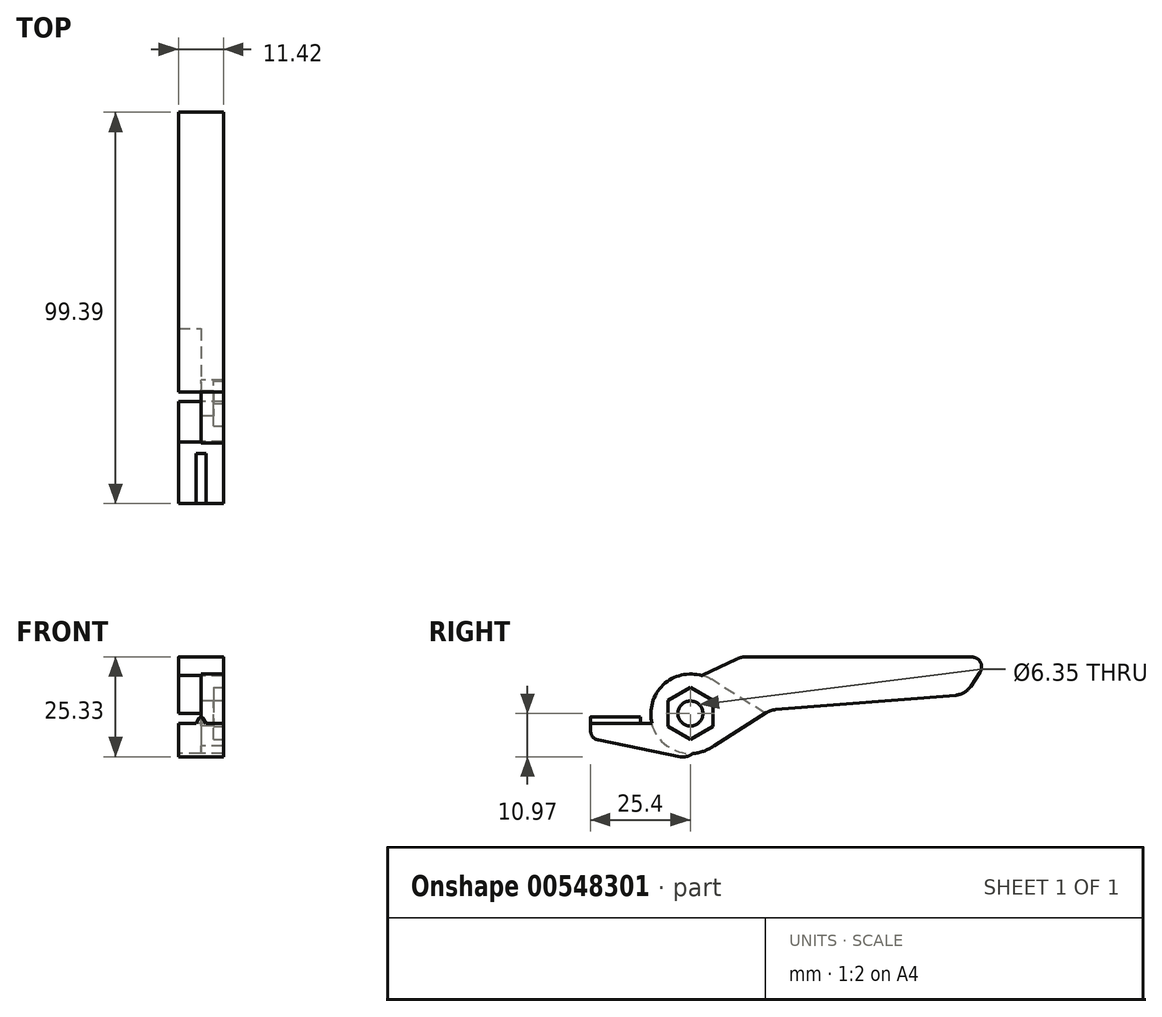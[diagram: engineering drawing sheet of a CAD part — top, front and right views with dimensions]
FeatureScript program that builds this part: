
annotation { "Feature Type Name" : "Feature", "Feature Type Description" : "" }
export const myFeature = defineFeature(function(context is Context, id is Id, definition is map)
    precondition{}
    {
        {
            var Q0;
            Q0=qCreatedBy(makeId("Right.planeOp"),FACE);
            var sketch = newSketch(context, id + "F0", { "sketchPlane" : qUnion([Q0])});
            skCircle(sketch, "E0", {"center": v(0, 0) * mm, "radius": 3.18 * mm});
            skArc(sketch, "E1", {"start": v(10.03, 0) * mm, "mid": v(-1.28, 9.95) * mm, "end": v(-9.7, -2.54) * mm});
            skLineSegment(sketch, "E2", {"start": v(-15.98, -2.54) * mm, "end": v(-8.82, -2.54) * mm});
            skArc(sketch, "E3", {"start": v(-9.84, -2.54) * mm, "mid": v(1.28, -10.08) * mm, "end": v(10.16, 0) * mm});
            skLineSegment(sketch, "E4", {"start": v(8.55, 0) * mm, "end": v(12.43, 0) * mm});
            skPoint(sketch, "E5.orphan", {"position": v(0, -10.03) * mm});
            skSolve(sketch);
        }
        {
            var Q0;
            Q0=qCreatedBy(makeId("Right.planeOp"),FACE);
            var sketch = newSketch(context, id + "F1", { "sketchPlane" : qUnion([Q0])});
            skLineSegment(sketch, "E6", {"start": v(9.3, 0) * mm, "end": v(10.16, 0.07) * mm});
            skLineSegment(sketch, "E7", {"start": v(69.85, 4.85) * mm, "end": v(76.2, 14.36) * mm});
            skCircle(sketch, "E8", {"center": v(0, 0) * mm, "radius": 10.16 * mm, "construction": true});
            skLineSegment(sketch, "E9", {"start": v(0, 0) * mm, "end": v(76.2, 0) * mm, "construction": true});
            skLineSegment(sketch, "E10", {"start": v(76.2, 14.36) * mm, "end": v(12.8, 14.36) * mm});
            skLineSegment(sketch, "E11", {"start": v(12.8, 14.36) * mm, "end": v(2.92, 9.73) * mm});
            skLineSegment(sketch, "E12", {"start": v(76.2, 14.36) * mm, "end": v(76.2, 0) * mm, "construction": true});
            skPoint(sketch, "E13.endSnap0", {"position": v(7.86, 12.04) * mm});
            skLineSegment(sketch, "E14", {"start": v(5.96, -8.23) * mm, "end": v(4.87, -6.63) * mm});
            skLineSegment(sketch, "E15", {"start": v(4.87, -6.63) * mm, "end": v(8.24, 1.75) * mm});
            skLineSegment(sketch, "E16", {"start": v(8.24, 1.75) * mm, "end": v(2.92, 9.73) * mm});
            skLineSegment(sketch, "E17.trimOffspring", {"start": v(20.4, 0.89) * mm, "end": v(69.85, 4.85) * mm});
            skLineSegment(sketch, "E18", {"start": v(20.4, 0.89) * mm, "end": v(5.96, -8.23) * mm});
            skSolve(sketch);
        }
        {
            var Q0;
            Q0 = qSketchRegion(id + "F1", true);
            extrude(context, id + "F2", {"entities" : qUnion([Q0]), "endBound" : BoundingType.SYMMETRIC, "depth" : 11.43 * mm, "offsetDistance" : 25.4 * mm});
        }
        {
            var Q0;
            Q0=makeQuery(id+"F2.opExtrude","SWEPT_EDGE",EDGE,{"disambiguationData":[OSD([sQuery(id+"F1.wireOp",EDGE,"E10"),sQuery(id+"F1.wireOp",EDGE,"E11")])]});
            var Q1;
            Q1=makeQuery(id+"F2.opExtrude","SWEPT_EDGE",EDGE,{"disambiguationData":[OSD([sQuery(id+"F1.wireOp",EDGE,"E7"),sQuery(id+"F1.wireOp",EDGE,"E17.trimOffspring")])]});
            var Q2;
            Q2=makeQuery(id+"F2.opExtrude","SWEPT_EDGE",EDGE,{"disambiguationData":[OSD([sQuery(id+"F1.wireOp",EDGE,"E17.trimOffspring"),sQuery(id+"F1.wireOp",EDGE,"E18")])]});
            fillet(context, id + "F3", {"entities" : qUnion([Q0, Q1, Q2]), "radius" : 5.08 * mm, "tangentPropagation" : true, "allowEdgeOverflow" : false});
        }
        {
            var Q0;
            Q0=makeQuery(id+"F2.opExtrude","SWEPT_EDGE",EDGE,{"disambiguationData":[OSD([sQuery(id+"F1.wireOp",EDGE,"E7"),sQuery(id+"F1.wireOp",EDGE,"E10")])]});
            fillet(context, id + "F4", {"entities" : qUnion([Q0]), "radius" : 2.54 * mm, "tangentPropagation" : true, "allowEdgeOverflow" : false});
        }
        {
            var Q0;
            Q0 = qSketchRegion(id + "F0", true);
            extrude(context, id + "F5", {"entities" : qUnion([Q0]), "operationType" : NewBodyOperationType.ADD, "depth" : 5.7 * mm, "offsetDistance" : 25.4 * mm});
        }
        {
            var Q0;
            Q0=qCreatedBy(makeId("Right.planeOp"),FACE);
            var sketch = newSketch(context, id + "F6", { "sketchPlane" : qUnion([Q0])});
            skArc(sketch, "E19", {"start": v(5.42, 8.6) * mm, "mid": v(-10.16, -0.1) * mm, "end": v(5.57, -8.5) * mm});
            skLineSegment(sketch, "E20", {"start": v(19.06, 0) * mm, "end": v(5.42, 8.6) * mm});
            skLineSegment(sketch, "E21", {"start": v(5.57, -8.5) * mm, "end": v(19.06, 0) * mm});
            skSolve(sketch);
        }
        {
            var Q0;
            Q0 = qSketchRegion(id + "F6", true);
            extrude(context, id + "F7", {"entities" : qUnion([Q0]), "operationType" : NewBodyOperationType.REMOVE, "oppositeDirection" : true, "depth" : 25.4 * mm, "offsetDistance" : 25.4 * mm});
        }
        {
            var Q0;
            Q0=qCreatedBy(makeId("Right.planeOp"),FACE);
            var sketch = newSketch(context, id + "F8", { "sketchPlane" : qUnion([Q0])});
            skCircle(sketch, "E22", {"center": v(0, 0) * mm, "radius": 10.16 * mm});
            skLineSegment(sketch, "E23", {"start": v(-9.84, 2.54) * mm, "end": v(-25.4, 2.54) * mm});
            skLineSegment(sketch, "E24", {"start": v(-25.4, 2.54) * mm, "end": v(-25.4, 6.36) * mm});
            skLineSegment(sketch, "E25", {"start": v(-25.4, 6.36) * mm, "end": v(-2.53, 10.97) * mm});
            skLineSegment(sketch, "E26", {"start": v(-2.53, 10.97) * mm, "end": v(7.5, 10.97) * mm});
            skLineSegment(sketch, "E27", {"start": v(7.5, 10.97) * mm, "end": v(4.02, 9.33) * mm});
            skLineSegment(sketch, "E28", {"start": v(0, 0) * mm, "end": v(-31.38, 0) * mm, "construction": true});
            skLineSegment(sketch, "E29.MirrorCS", {"start": v(-9.84, -2.54) * mm, "end": v(-25.4, -2.54) * mm});
            skLineSegment(sketch, "E30.MirrorCS", {"start": v(-25.4, -2.54) * mm, "end": v(-25.4, -6.36) * mm});
            skLineSegment(sketch, "E31.MirrorCS", {"start": v(-25.4, -6.36) * mm, "end": v(-2.53, -10.97) * mm});
            skLineSegment(sketch, "E32.MirrorCS", {"start": v(-2.53, -10.97) * mm, "end": v(7.5, -10.97) * mm});
            skLineSegment(sketch, "E33.MirrorCS", {"start": v(7.5, -10.97) * mm, "end": v(4.02, -9.33) * mm});
            skLineSegment(sketch, "E34", {"start": v(0.54, -10.15) * mm, "end": v(0.54, -10.97) * mm});
            skSolve(sketch);
        }
        {
            var Q0;
            {var subQ0=sQuery(id+"F8.wireOp",EDGE,"E29.MirrorCS");Q0=makeQuery(id+"F8.imprint","IMPRINT",FACE,{"disambiguationData":[TD([[makeQuery(id+"F8.imprint","IMPRINT",EDGE,{"derivedFrom":subQ0}),1.0]])]});}
            extrude(context, id + "F9", {"entities" : qUnion([Q0]), "operationType" : NewBodyOperationType.ADD, "endBound" : BoundingType.SYMMETRIC, "depth" : 11.43 * mm, "offsetDistance" : 25.4 * mm});
        }
        {
            var Q0;
            Q0=makeQuery(id+"F9.opExtrude","SWEPT_EDGE",EDGE,{"disambiguationData":[OSD([sQuery(id+"F8.wireOp",EDGE,"E32.MirrorCS"),sQuery(id+"F8.wireOp",EDGE,"E34")])]});
            var Q1;
            Q1=makeQuery(id+"F9.opExtrude","SWEPT_EDGE",EDGE,{"disambiguationData":[OSD([sQuery(id+"F8.wireOp",EDGE,"E30.MirrorCS"),sQuery(id+"F8.wireOp",EDGE,"E31.MirrorCS")])]});
            fillet(context, id + "F10", {"entities" : qUnion([Q0, Q1]), "radius" : 2.54 * mm, "tangentPropagation" : true, "allowEdgeOverflow" : false});
        }
        {
            var Q0;
            Q0=makeQuery(id+"F9.opExtrude","SWEPT_FACE",FACE,{"disambiguationData":[OSD([sQuery(id+"F8.wireOp",EDGE,"E30.MirrorCS")])]});
            var sketch = newSketch(context, id + "F11", { "sketchPlane" : qUnion([Q0])});
            skLineSegment(sketch, "E35", {"start": v(-1.27, -2.54) * mm, "end": v(0, -0.41) * mm});
            skLineSegment(sketch, "E36", {"start": v(0, -0.41) * mm, "end": v(1.27, -2.54) * mm});
            skLineSegment(sketch, "E37", {"start": v(1.27, -2.54) * mm, "end": v(-1.27, -2.54) * mm});
            skSolve(sketch);
        }
        {
            var Q0;
            Q0 = qSketchRegion(id + "F11", true);
            extrude(context, id + "F12", {"entities" : qUnion([Q0]), "operationType" : NewBodyOperationType.ADD, "oppositeDirection" : true, "depth" : 12.7 * mm, "offsetDistance" : 25.4 * mm});
        }
        {
            var Q0;
            Q0=makeQuery(id+"F12.opExtrude","SWEPT_EDGE",EDGE,{"disambiguationData":[OSD([sQuery(id+"F11.wireOp",EDGE,"E35"),sQuery(id+"F11.wireOp",EDGE,"E36")])]});
            fillet(context, id + "F13", {"entities" : qUnion([Q0]), "radius" : 0.5 * mm, "tangentPropagation" : true, "allowEdgeOverflow" : false});
        }
        {
            var Q0;
            Q0=makeQuery(id+"F9.boolean.opBoolean","MERGE",FACE,{"derivedFrom":[makeQuery(id+"F5.boolean.opBoolean","MERGE",FACE,{"derivedFrom":[makeQuery(id+"F2.opExtrude","CAP_FACE",FACE,{"disambiguationData":[OSD([sQuery(id+"F1.wireOp",EDGE,"E7"),sQuery(id+"F1.wireOp",EDGE,"E10"),sQuery(id+"F1.wireOp",EDGE,"E11"),sQuery(id+"F1.wireOp",EDGE,"E14"),sQuery(id+"F1.wireOp",EDGE,"E15"),sQuery(id+"F1.wireOp",EDGE,"E16"),sQuery(id+"F1.wireOp",EDGE,"E17.trimOffspring"),sQuery(id+"F1.wireOp",EDGE,"E18")])],"isStart":false}),makeQuery(id+"F5.opExtrude","CAP_FACE",FACE,{"disambiguationData":[OSD([sQuery(id+"F0.wireOp",EDGE,"E0"),sQuery(id+"F0.wireOp",EDGE,"E1")])],"isStart":false})]}),makeQuery(id+"F9.opExtrude","CAP_FACE",FACE,{"disambiguationData":[OSD([sQuery(id+"F8.wireOp",EDGE,"E22"),sQuery(id+"F8.wireOp",EDGE,"E29.MirrorCS"),sQuery(id+"F8.wireOp",EDGE,"E30.MirrorCS"),sQuery(id+"F8.wireOp",EDGE,"E31.MirrorCS"),sQuery(id+"F8.wireOp",EDGE,"E32.MirrorCS"),sQuery(id+"F8.wireOp",EDGE,"E34")])],"isStart":false})]});
            var sketch = newSketch(context, id + "F14", { "sketchPlane" : qUnion([Q0])});
            skCircle(sketch, "E38.cCircle", {"center": v(0, 0) * mm, "radius": 5.72 * mm, "construction": true});
            skLineSegment(sketch, "E38.0", {"start": v(5.72, 3.3) * mm, "end": v(5.72, -3.3) * mm});
            skLineSegment(sketch, "E38.1", {"start": v(5.72, -3.3) * mm, "end": v(0, -6.6) * mm});
            skLineSegment(sketch, "E38.2", {"start": v(0, -6.6) * mm, "end": v(-5.71, -3.3) * mm});
            skLineSegment(sketch, "E38.3", {"start": v(-5.71, -3.3) * mm, "end": v(-5.72, 3.3) * mm});
            skLineSegment(sketch, "E38.4", {"start": v(-5.72, 3.3) * mm, "end": v(0, 6.6) * mm});
            skLineSegment(sketch, "E38.5", {"start": v(0, 6.6) * mm, "end": v(5.72, 3.3) * mm});
            skPoint(sketch, "E38.0.midPoint", {"position": v(5.72, 0) * mm});
            skSolve(sketch);
        }
        {
            var Q0;
            Q0 = qSketchRegion(id + "F14", true);
            extrude(context, id + "F15", {"entities" : qUnion([Q0]), "operationType" : NewBodyOperationType.REMOVE, "oppositeDirection" : true, "depth" : 2.54 * mm, "offsetDistance" : 25.4 * mm});
        }
    });
